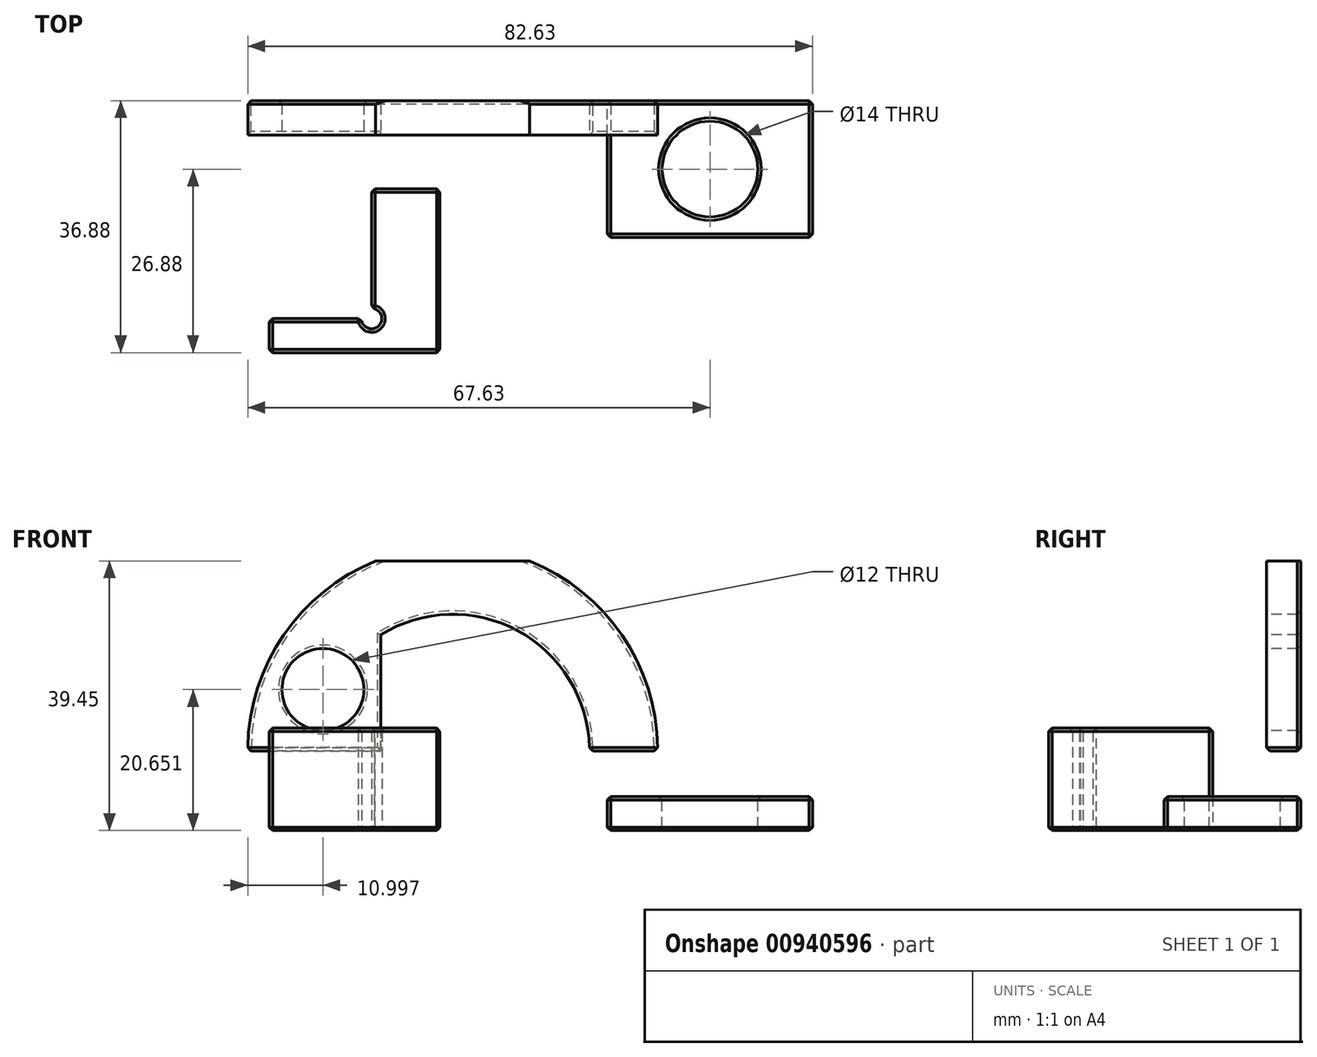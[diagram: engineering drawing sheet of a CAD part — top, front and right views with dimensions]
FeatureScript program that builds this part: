
annotation { "Feature Type Name" : "Feature", "Feature Type Description" : "" }
export const myFeature = defineFeature(function(context is Context, id is Id, definition is map)
    precondition{}
    {
        {
            var Q0;
            Q0=qCreatedBy(makeId("Front.planeOp"),FACE);
            var sketch = newSketch(context, id + "F0", { "sketchPlane" : qUnion([Q0])});
            skLineSegment(sketch, "E0.bottom", {"start": v(0, 0) * mm, "end": v(30, 0) * mm});
            skLineSegment(sketch, "E0.top", {"start": v(0, 5) * mm, "end": v(30, 5) * mm});
            skLineSegment(sketch, "E0.left", {"start": v(0, 0) * mm, "end": v(0, 5) * mm});
            skLineSegment(sketch, "E0.right", {"start": v(30, 0) * mm, "end": v(30, 5) * mm});
            skSolve(sketch);
        }
        {
            var Q0;
            Q0=makeQuery(id+"F0.imprint","IMPRINT",FACE,{"disambiguationData":[TD([[makeQuery(id+"F0.imprint","IMPRINT",EDGE,{"derivedFrom":sQuery(id+"F0.wireOp",EDGE,"E0.bottom")}),1.0]])]});
            extrude(context, id + "F1", {"entities" : qUnion([Q0]), "depth" : 20 * mm, "offsetDistance" : 25 * mm});
        }
        {
            var Q0;
            Q0=qCreatedBy(makeId("Front.planeOp"),FACE);
            var sketch = newSketch(context, id + "F2", { "sketchPlane" : qUnion([Q0])});
            skLineSegment(sketch, "E1.bottom", {"start": v(-52.63, 11.65) * mm, "end": v(7.37, 11.65) * mm});
            skLineSegment(sketch, "E1.top", {"start": v(-52.63, 39.45) * mm, "end": v(7.37, 39.45) * mm});
            skLineSegment(sketch, "E1.left", {"start": v(-52.63, 11.65) * mm, "end": v(-52.63, 39.45) * mm});
            skLineSegment(sketch, "E1.right", {"start": v(7.37, 11.65) * mm, "end": v(7.37, 39.45) * mm});
            skSolve(sketch);
        }
        {
            var Q0;
            Q0 = qSketchRegion(id + "F2", true);
            extrude(context, id + "F3", {"entities" : qUnion([Q0]), "depth" : 5 * mm, "offsetDistance" : 25 * mm});
        }
        {
            var Q0;
            Q0=makeQuery(id+"F3.opExtrude","CAP_FACE",FACE,{"disambiguationData":[OSD([sQuery(id+"F2.wireOp",EDGE,"E1.bottom"),sQuery(id+"F2.wireOp",EDGE,"E1.top"),sQuery(id+"F2.wireOp",EDGE,"E1.left"),sQuery(id+"F2.wireOp",EDGE,"E1.right")])],"isStart":false});
            var sketch = newSketch(context, id + "F4", { "sketchPlane" : qUnion([Q0])});
            skCircle(sketch, "E2", {"center": v(-22.63, 11.65) * mm, "radius": 20 * mm});
            skCircle(sketch, "E3", {"center": v(-22.63, 11.65) * mm, "radius": 30 * mm});
            skLineSegment(sketch, "E4", {"start": v(-33.17, 28.65) * mm, "end": v(-33.17, 11.65) * mm});
            skLineSegment(sketch, "E5", {"start": v(-33.17, 11.65) * mm, "end": v(-42.63, 11.65) * mm});
            skCircle(sketch, "E6", {"center": v(-41.63, 20.65) * mm, "radius": 6 * mm});
            skSolve(sketch);
        }
        {
            var Q0;
            {var subQ0=sQuery(id+"F4.wireOp",EDGE,"E2");var subQ1=makeQuery(id+"F3.opExtrude","CAP_EDGE",EDGE,{"disambiguationData":[OSD([sQuery(id+"F2.wireOp",EDGE,"E1.bottom")])],"isStart":false});var subQ2=makeQuery(id+"F4.imprint","INTERSECT",VERTEX,{"disambiguationData":[OD(0.0)],"derivedFrom":[subQ1,subQ0]});Q0=makeQuery(id+"F4.imprint","IMPRINT",FACE,{"disambiguationData":[TD([[makeQuery(id+"F4.imprint","IMPRINT",EDGE,{"disambiguationData":[TD([[subQ2,-1.0]])],"derivedFrom":subQ0}),1.0]])]});}
            var Q1;
            {var subQ0=sQuery(id+"F4.wireOp",EDGE,"E2");var subQ1=makeQuery(id+"F3.opExtrude","CAP_EDGE",EDGE,{"disambiguationData":[OSD([sQuery(id+"F2.wireOp",EDGE,"E1.bottom")])],"isStart":false});var subQ2=makeQuery(id+"F4.imprint","INTERSECT",VERTEX,{"disambiguationData":[OD(0.0)],"derivedFrom":[subQ1,subQ0]});Q1=makeQuery(id+"F4.imprint","IMPRINT",FACE,{"disambiguationData":[TD([[makeQuery(id+"F4.imprint","IMPRINT",EDGE,{"disambiguationData":[TD([[subQ2,1.0]])],"derivedFrom":subQ0}),1.0]])]});}
            var Q2;
            {var subQ1=makeQuery(id+"F3.opExtrude","CAP_EDGE",EDGE,{"disambiguationData":[OSD([sQuery(id+"F2.wireOp",EDGE,"E1.left")])],"isStart":false});Q2=makeQuery(id+"F4.imprint","IMPRINT",FACE,{"disambiguationData":[TD([[makeQuery(id+"F4.imprint","IMPRINT",EDGE,{"derivedFrom":subQ1}),-1.0]])]});}
            var Q3;
            {var subQ1=makeQuery(id+"F3.opExtrude","CAP_EDGE",EDGE,{"disambiguationData":[OSD([sQuery(id+"F2.wireOp",EDGE,"E1.right")])],"isStart":false});Q3=makeQuery(id+"F4.imprint","IMPRINT",FACE,{"disambiguationData":[TD([[makeQuery(id+"F4.imprint","IMPRINT",EDGE,{"derivedFrom":subQ1}),1.0]])]});}
            var Q4;
            {var subQ0=sQuery(id+"F4.wireOp",EDGE,"E6");var subQ1=sQuery(id+"F4.wireOp",EDGE,"E2");var subQ2=makeQuery(id+"F4.imprint","INTERSECT",VERTEX,{"disambiguationData":[OD(0.0)],"derivedFrom":[subQ1,subQ0]});Q4=makeQuery(id+"F4.imprint","IMPRINT",FACE,{"disambiguationData":[TD([[makeQuery(id+"F4.imprint","IMPRINT",EDGE,{"disambiguationData":[TD([[subQ2,-1.0]])],"derivedFrom":subQ1}),1.0]])]});}
            var Q5;
            {var subQ0=sQuery(id+"F4.wireOp",EDGE,"E6");var subQ1=sQuery(id+"F4.wireOp",EDGE,"E2");var subQ2=makeQuery(id+"F4.imprint","INTERSECT",VERTEX,{"disambiguationData":[OD(0.0)],"derivedFrom":[subQ1,subQ0]});Q5=makeQuery(id+"F4.imprint","IMPRINT",FACE,{"disambiguationData":[TD([[makeQuery(id+"F4.imprint","IMPRINT",EDGE,{"disambiguationData":[TD([[subQ2,-1.0]])],"derivedFrom":subQ1}),-1.0]])]});}
            extrude(context, id + "F5", {"entities" : qUnion([Q0, Q1, Q2, Q3, Q4, Q5]), "operationType" : NewBodyOperationType.REMOVE, "oppositeDirection" : true, "depth" : 25 * mm, "offsetDistance" : 25 * mm});
        }
        {
            var Q0;
            Q0=qCreatedBy(makeId("Top.planeOp"),FACE);
            var sketch = newSketch(context, id + "F6", { "sketchPlane" : qUnion([Q0])});
            skLineSegment(sketch, "E7.bottom", {"start": v(-49.5, -36.88) * mm, "end": v(-24.5, -36.88) * mm});
            skLineSegment(sketch, "E7.top", {"start": v(-34.5, -12.88) * mm, "end": v(-24.5, -12.88) * mm});
            skLineSegment(sketch, "E7.left", {"start": v(-49.5, -36.88) * mm, "end": v(-49.5, -31.88) * mm});
            skLineSegment(sketch, "E7.right", {"start": v(-24.5, -36.88) * mm, "end": v(-24.5, -12.88) * mm});
            skLineSegment(sketch, "E8.top", {"start": v(-49.5, -31.88) * mm, "end": v(-36, -31.88) * mm});
            skLineSegment(sketch, "E8.right", {"start": v(-34.5, -12.88) * mm, "end": v(-34.5, -30.38) * mm});
            skArc(sketch, "E9", {"start": v(-36, -31.88) * mm, "mid": v(-33.45, -32.94) * mm, "end": v(-34.5, -30.38) * mm});
            skSolve(sketch);
        }
        {
            var Q0;
            Q0=makeQuery(id+"F6.imprint","IMPRINT",FACE,{"disambiguationData":[TD([[makeQuery(id+"F6.imprint","IMPRINT",EDGE,{"derivedFrom":sQuery(id+"F6.wireOp",EDGE,"E7.bottom")}),1.0]])]});
            extrude(context, id + "F7", {"entities" : qUnion([Q0]), "depth" : 15 * mm, "offsetDistance" : 25 * mm});
        }
        {
            var Q0;
            Q0=makeQuery(id+"F1.opExtrude","SWEPT_FACE",FACE,{"disambiguationData":[OSD([sQuery(id+"F0.wireOp",EDGE,"E0.top")])]});
            var sketch = newSketch(context, id + "F8", { "sketchPlane" : qUnion([Q0])});
            skCircle(sketch, "E10", {"center": v(15, -10) * mm, "radius": 7 * mm});
            skSolve(sketch);
        }
        {
            var Q0;
            Q0=makeQuery(id+"F8.imprint","IMPRINT",FACE,{"disambiguationData":[TD([[makeQuery(id+"F8.imprint","IMPRINT",EDGE,{"derivedFrom":sQuery(id+"F8.wireOp",EDGE,"E10")}),1.0]])]});
            extrude(context, id + "F9", {"entities" : qUnion([Q0]), "operationType" : NewBodyOperationType.REMOVE, "oppositeDirection" : true, "depth" : 25 * mm, "offsetDistance" : 25 * mm});
        }
        {
            var Q0;
            Q0=makeQuery(id+"F1.opExtrude","SWEPT_FACE",FACE,{"disambiguationData":[OSD([sQuery(id+"F0.wireOp",EDGE,"E0.bottom")])]});
            var Q1;
            Q1=makeQuery(id+"F1.opExtrude","SWEPT_EDGE",EDGE,{"disambiguationData":[OSD([sQuery(id+"F0.wireOp",EDGE,"E0.bottom"),sQuery(id+"F0.wireOp",EDGE,"E0.right")])]});
            var Q2;
            Q2=makeQuery(id+"F1.opExtrude","CAP_FACE",FACE,{"disambiguationData":[OSD([sQuery(id+"F0.wireOp",EDGE,"E0.bottom"),sQuery(id+"F0.wireOp",EDGE,"E0.top"),sQuery(id+"F0.wireOp",EDGE,"E0.left"),sQuery(id+"F0.wireOp",EDGE,"E0.right")])],"isStart":true});
            var Q3;
            Q3=makeQuery(id+"F1.opExtrude","SWEPT_EDGE",EDGE,{"disambiguationData":[OSD([sQuery(id+"F0.wireOp",EDGE,"E0.top"),sQuery(id+"F0.wireOp",EDGE,"E0.left")])]});
            var Q4;
            Q4=makeQuery(id+"F1.opExtrude","CAP_FACE",FACE,{"disambiguationData":[OSD([sQuery(id+"F0.wireOp",EDGE,"E0.bottom"),sQuery(id+"F0.wireOp",EDGE,"E0.top"),sQuery(id+"F0.wireOp",EDGE,"E0.left"),sQuery(id+"F0.wireOp",EDGE,"E0.right")])],"isStart":false});
            var Q5;
            Q5=makeQuery(id+"F1.opExtrude","SWEPT_EDGE",EDGE,{"disambiguationData":[OSD([sQuery(id+"F0.wireOp",EDGE,"E0.top"),sQuery(id+"F0.wireOp",EDGE,"E0.right")])]});
            var Q6;
            Q6=makeQuery(id+"F1.opExtrude","SWEPT_FACE",FACE,{"disambiguationData":[OSD([sQuery(id+"F0.wireOp",EDGE,"E0.top")])]});
            var Q7;
            Q7=makeQuery(id+"F1.opExtrude","SWEPT_FACE",FACE,{"disambiguationData":[OSD([sQuery(id+"F0.wireOp",EDGE,"E0.left")])]});
            var Q8;
            Q8=makeQuery(id+"F1.opExtrude","SWEPT_FACE",FACE,{"disambiguationData":[OSD([sQuery(id+"F0.wireOp",EDGE,"E0.right")])]});
            var Q9;
            Q9=makeQuery(id+"F1.opExtrude","CAP_EDGE",EDGE,{"disambiguationData":[OSD([sQuery(id+"F0.wireOp",EDGE,"E0.top")])],"isStart":true});
            var Q10;
            Q10=makeQuery(id+"F1.opExtrude","CAP_EDGE",EDGE,{"disambiguationData":[OSD([sQuery(id+"F0.wireOp",EDGE,"E0.top")])],"isStart":false});
            var Q11;
            Q11=makeQuery(id+"F1.opExtrude","SWEPT_EDGE",EDGE,{"disambiguationData":[OSD([sQuery(id+"F0.wireOp",EDGE,"E0.bottom"),sQuery(id+"F0.wireOp",EDGE,"E0.left")])]});
            var Q12;
            Q12=makeQuery(id+"F1.opExtrude","CAP_EDGE",EDGE,{"disambiguationData":[OSD([sQuery(id+"F0.wireOp",EDGE,"E0.bottom")])],"isStart":true});
            var Q13;
            Q13=makeQuery(id+"F1.opExtrude","CAP_EDGE",EDGE,{"disambiguationData":[OSD([sQuery(id+"F0.wireOp",EDGE,"E0.bottom")])],"isStart":false});
            var Q14;
            Q14=makeQuery(id+"F1.opExtrude","CAP_EDGE",EDGE,{"disambiguationData":[OSD([sQuery(id+"F0.wireOp",EDGE,"E0.left")])],"isStart":true});
            var Q15;
            Q15=makeQuery(id+"F1.opExtrude","CAP_EDGE",EDGE,{"disambiguationData":[OSD([sQuery(id+"F0.wireOp",EDGE,"E0.left")])],"isStart":false});
            var Q16;
            Q16=makeQuery(id+"F1.opExtrude","CAP_EDGE",EDGE,{"disambiguationData":[OSD([sQuery(id+"F0.wireOp",EDGE,"E0.right")])],"isStart":true});
            var Q17;
            Q17=makeQuery(id+"F1.opExtrude","CAP_EDGE",EDGE,{"disambiguationData":[OSD([sQuery(id+"F0.wireOp",EDGE,"E0.right")])],"isStart":false});
            var Q18;
            {var subQ0=sQuery(id+"F4.wireOp",EDGE,"E3");var subQ1=sQuery(id+"F2.wireOp",EDGE,"E1.left");var subQ2=sQuery(id+"F2.wireOp",EDGE,"E1.bottom");var subQ3=sQuery(id+"F2.wireOp",EDGE,"E1.top");Q18=makeQuery(id+"F5.boolean.opBoolean","INTERSECT",EDGE,{"derivedFrom":[makeQuery(id+"F3.opExtrude","CAP_FACE",FACE,{"disambiguationData":[OSD([subQ2,subQ3,subQ1,sQuery(id+"F2.wireOp",EDGE,"E1.right")])],"isStart":true}),makeQuery(id+"F5.opExtrude","SWEPT_FACE",FACE,{"disambiguationData":[OSD([subQ0]),TDD([makeQuery(id+"F4.imprint","IMPRINT",EDGE,{"disambiguationData":[TD([[makeQuery(id+"F4.imprint","INTERSECT",VERTEX,{"disambiguationData":[OD(1.0)],"derivedFrom":[makeQuery(id+"F3.opExtrude","CAP_EDGE",EDGE,{"disambiguationData":[OSD([subQ3])],"isStart":false}),subQ0]}),-1.0]])],"derivedFrom":subQ0})])]})]});}
            var Q19;
            Q19=makeQuery(id+"F5.boolean.opBoolean","INTERSECT",EDGE,{"derivedFrom":[makeQuery(id+"F3.opExtrude","CAP_FACE",FACE,{"disambiguationData":[OSD([sQuery(id+"F2.wireOp",EDGE,"E1.bottom"),sQuery(id+"F2.wireOp",EDGE,"E1.top"),sQuery(id+"F2.wireOp",EDGE,"E1.left"),sQuery(id+"F2.wireOp",EDGE,"E1.right")])],"isStart":true}),makeQuery(id+"F5.opExtrude","SWEPT_FACE",FACE,{"disambiguationData":[OSD([sQuery(id+"F4.wireOp",EDGE,"E2")])]})]});
            var Q20;
            {var subQ0=sQuery(id+"F4.wireOp",EDGE,"E3");var subQ1=sQuery(id+"F2.wireOp",EDGE,"E1.top");Q20=makeQuery(id+"F5.boolean.opBoolean","COPY",EDGE,{"derivedFrom":makeQuery(id+"F5.opExtrude","SWEPT_EDGE",EDGE,{"disambiguationData":[OSD([subQ1,subQ0]),TDD([makeQuery(id+"F4.imprint","INTERSECT",VERTEX,{"disambiguationData":[OD(1.0)],"derivedFrom":[makeQuery(id+"F3.opExtrude","CAP_EDGE",EDGE,{"disambiguationData":[OSD([subQ1])],"isStart":false}),subQ0]})])]})});}
            var Q21;
            {var subQ0=sQuery(id+"F4.wireOp",EDGE,"E3");Q21=makeQuery(id+"F5.boolean.opBoolean","COPY",EDGE,{"derivedFrom":makeQuery(id+"F5.opExtrude","CAP_EDGE",EDGE,{"disambiguationData":[OSD([subQ0]),TDD([makeQuery(id+"F4.imprint","IMPRINT",EDGE,{"disambiguationData":[TD([[makeQuery(id+"F4.imprint","INTERSECT",VERTEX,{"disambiguationData":[OD(1.0)],"derivedFrom":[makeQuery(id+"F3.opExtrude","CAP_EDGE",EDGE,{"disambiguationData":[OSD([sQuery(id+"F2.wireOp",EDGE,"E1.top")])],"isStart":false}),subQ0]}),-1.0]])],"derivedFrom":subQ0})])],"isStart":true})});}
            var Q22;
            {var subQ0=sQuery(id+"F4.wireOp",EDGE,"E3");Q22=makeQuery(id+"F5.boolean.opBoolean","COPY",EDGE,{"derivedFrom":makeQuery(id+"F5.opExtrude","CAP_EDGE",EDGE,{"disambiguationData":[OSD([subQ0]),TDD([makeQuery(id+"F4.imprint","IMPRINT",EDGE,{"disambiguationData":[TD([[makeQuery(id+"F4.imprint","INTERSECT",VERTEX,{"disambiguationData":[OD(0.0)],"derivedFrom":[makeQuery(id+"F3.opExtrude","CAP_EDGE",EDGE,{"disambiguationData":[OSD([sQuery(id+"F2.wireOp",EDGE,"E1.top")])],"isStart":false}),subQ0]}),1.0]])],"derivedFrom":subQ0})])],"isStart":true})});}
            var Q23;
            Q23=makeQuery(id+"F5.boolean.opBoolean","COPY",EDGE,{"derivedFrom":makeQuery(id+"F5.opExtrude","CAP_EDGE",EDGE,{"disambiguationData":[OSD([sQuery(id+"F4.wireOp",EDGE,"E2")])],"isStart":true})});
            var Q24;
            {var subQ0=sQuery(id+"F2.wireOp",EDGE,"E1.left");var subQ1=sQuery(id+"F2.wireOp",EDGE,"E1.bottom");Q24=makeQuery(id+"F5.boolean.opBoolean","MERGE",EDGE,{"derivedFrom":[makeQuery(id+"F3.opExtrude","SWEPT_EDGE",EDGE,{"disambiguationData":[OSD([subQ1,subQ0])]})],"fromTools":[makeQuery(id+"F5.opExtrude","SWEPT_EDGE",EDGE,{"disambiguationData":[OSD([subQ1,subQ0,sQuery(id+"F4.wireOp",EDGE,"E3")])]})]});}
            var Q25;
            Q25=makeQuery(id+"F5.boolean.opBoolean","INTERSECT",EDGE,{"disambiguationData":[OD(0.0)],"derivedFrom":[makeQuery(id+"F3.opExtrude","SWEPT_FACE",FACE,{"disambiguationData":[OSD([sQuery(id+"F2.wireOp",EDGE,"E1.bottom")])]}),makeQuery(id+"F5.opExtrude","SWEPT_FACE",FACE,{"disambiguationData":[OSD([sQuery(id+"F4.wireOp",EDGE,"E2")])]})]});
            var Q26;
            Q26=makeQuery(id+"F5.boolean.opBoolean","INTERSECT",EDGE,{"disambiguationData":[OD(1.0)],"derivedFrom":[makeQuery(id+"F3.opExtrude","SWEPT_FACE",FACE,{"disambiguationData":[OSD([sQuery(id+"F2.wireOp",EDGE,"E1.bottom")])]}),makeQuery(id+"F5.opExtrude","SWEPT_FACE",FACE,{"disambiguationData":[OSD([sQuery(id+"F4.wireOp",EDGE,"E2")])]})]});
            var Q27;
            {var subQ0=sQuery(id+"F4.wireOp",EDGE,"E3");var subQ1=sQuery(id+"F2.wireOp",EDGE,"E1.top");Q27=makeQuery(id+"F5.boolean.opBoolean","COPY",EDGE,{"derivedFrom":makeQuery(id+"F5.opExtrude","SWEPT_EDGE",EDGE,{"disambiguationData":[OSD([subQ1,subQ0]),TDD([makeQuery(id+"F4.imprint","INTERSECT",VERTEX,{"disambiguationData":[OD(0.0)],"derivedFrom":[makeQuery(id+"F3.opExtrude","CAP_EDGE",EDGE,{"disambiguationData":[OSD([subQ1])],"isStart":false}),subQ0]})])]})});}
            var Q28;
            {var subQ0=sQuery(id+"F4.wireOp",EDGE,"E3");var subQ1=sQuery(id+"F2.wireOp",EDGE,"E1.right");var subQ2=sQuery(id+"F2.wireOp",EDGE,"E1.bottom");var subQ3=sQuery(id+"F2.wireOp",EDGE,"E1.top");Q28=makeQuery(id+"F5.boolean.opBoolean","INTERSECT",EDGE,{"derivedFrom":[makeQuery(id+"F3.opExtrude","CAP_FACE",FACE,{"disambiguationData":[OSD([subQ2,subQ3,sQuery(id+"F2.wireOp",EDGE,"E1.left"),subQ1])],"isStart":true}),makeQuery(id+"F5.opExtrude","SWEPT_FACE",FACE,{"disambiguationData":[OSD([subQ0]),TDD([makeQuery(id+"F4.imprint","IMPRINT",EDGE,{"disambiguationData":[TD([[makeQuery(id+"F4.imprint","INTERSECT",VERTEX,{"disambiguationData":[OD(0.0)],"derivedFrom":[makeQuery(id+"F3.opExtrude","CAP_EDGE",EDGE,{"disambiguationData":[OSD([subQ3])],"isStart":false}),subQ0]}),1.0]])],"derivedFrom":subQ0})])]})]});}
            var Q29;
            {var subQ0=sQuery(id+"F2.wireOp",EDGE,"E1.right");var subQ1=sQuery(id+"F2.wireOp",EDGE,"E1.bottom");Q29=makeQuery(id+"F5.boolean.opBoolean","MERGE",EDGE,{"derivedFrom":[makeQuery(id+"F3.opExtrude","SWEPT_EDGE",EDGE,{"disambiguationData":[OSD([subQ1,subQ0])]})],"fromTools":[makeQuery(id+"F5.opExtrude","SWEPT_EDGE",EDGE,{"disambiguationData":[OSD([subQ1,subQ0,sQuery(id+"F4.wireOp",EDGE,"E3")])]})]});}
            var Q30;
            Q30=makeQuery(id+"F7.opExtrude","CAP_EDGE",EDGE,{"disambiguationData":[OSD([sQuery(id+"F6.wireOp",EDGE,"E9")])],"isStart":false});
            var Q31;
            Q31=makeQuery(id+"F7.opExtrude","SWEPT_EDGE",EDGE,{"disambiguationData":[OSD([sQuery(id+"F6.wireOp",EDGE,"E7.top"),sQuery(id+"F6.wireOp",EDGE,"E7.right")])]});
            var Q32;
            Q32=makeQuery(id+"F7.opExtrude","SWEPT_EDGE",EDGE,{"disambiguationData":[OSD([sQuery(id+"F6.wireOp",EDGE,"E7.bottom"),sQuery(id+"F6.wireOp",EDGE,"E7.right")])]});
            var Q33;
            Q33=makeQuery(id+"F7.opExtrude","SWEPT_EDGE",EDGE,{"disambiguationData":[OSD([sQuery(id+"F6.wireOp",EDGE,"E7.bottom"),sQuery(id+"F6.wireOp",EDGE,"E7.left")])]});
            var Q34;
            {var subQ0=sQuery(id+"F2.wireOp",EDGE,"E1.bottom");var subQ2=sQuery(id+"F2.wireOp",EDGE,"E1.top");var subQ3=sQuery(id+"F4.wireOp",EDGE,"E3");var subQ4=makeQuery(id+"F3.opExtrude","CAP_EDGE",EDGE,{"disambiguationData":[OSD([subQ0])],"isStart":false});Q34=makeQuery(id+"F5.boolean.opBoolean","SPLIT",EDGE,{"disambiguationData":[TD([makeQuery(id+"F5.opExtrude","SWEPT_FACE",FACE,{"disambiguationData":[OSD([subQ3]),TDD([makeQuery(id+"F4.imprint","IMPRINT",EDGE,{"disambiguationData":[TD([[makeQuery(id+"F4.imprint","INTERSECT",VERTEX,{"disambiguationData":[OD(1.0)],"derivedFrom":[makeQuery(id+"F3.opExtrude","CAP_EDGE",EDGE,{"disambiguationData":[OSD([subQ2])],"isStart":false}),subQ3]}),-1.0]])],"derivedFrom":subQ3})])]})])],"derivedFrom":subQ4});}
            var Q35;
            Q35=makeQuery(id+"F7.opExtrude","CAP_EDGE",EDGE,{"disambiguationData":[OSD([sQuery(id+"F6.wireOp",EDGE,"E8.right")])],"isStart":false});
            var Q36;
            Q36=makeQuery(id+"F7.opExtrude","CAP_EDGE",EDGE,{"disambiguationData":[OSD([sQuery(id+"F6.wireOp",EDGE,"E7.right")])],"isStart":false});
            var Q37;
            Q37=makeQuery(id+"F7.opExtrude","SWEPT_EDGE",EDGE,{"disambiguationData":[OSD([sQuery(id+"F6.wireOp",EDGE,"E7.top"),sQuery(id+"F6.wireOp",EDGE,"E8.right")])]});
            var Q38;
            Q38=makeQuery(id+"F7.opExtrude","CAP_EDGE",EDGE,{"disambiguationData":[OSD([sQuery(id+"F6.wireOp",EDGE,"E7.left")])],"isStart":false});
            var Q39;
            Q39=makeQuery(id+"F7.opExtrude","CAP_EDGE",EDGE,{"disambiguationData":[OSD([sQuery(id+"F6.wireOp",EDGE,"E8.top")])],"isStart":false});
            var Q40;
            Q40=makeQuery(id+"F7.opExtrude","CAP_EDGE",EDGE,{"disambiguationData":[OSD([sQuery(id+"F6.wireOp",EDGE,"E7.bottom")])],"isStart":false});
            var Q41;
            Q41=makeQuery(id+"F7.opExtrude","SWEPT_EDGE",EDGE,{"disambiguationData":[OSD([sQuery(id+"F6.wireOp",EDGE,"E7.left"),sQuery(id+"F6.wireOp",EDGE,"E8.top")])]});
            var Q42;
            Q42=makeQuery(id+"F7.opExtrude","CAP_EDGE",EDGE,{"disambiguationData":[OSD([sQuery(id+"F6.wireOp",EDGE,"E7.bottom")])],"isStart":true});
            var Q43;
            Q43=makeQuery(id+"F7.opExtrude","CAP_EDGE",EDGE,{"disambiguationData":[OSD([sQuery(id+"F6.wireOp",EDGE,"E7.left")])],"isStart":true});
            var Q44;
            Q44=makeQuery(id+"F7.opExtrude","SWEPT_EDGE",EDGE,{"disambiguationData":[OSD([sQuery(id+"F6.wireOp",EDGE,"E8.top"),sQuery(id+"F6.wireOp",EDGE,"E9")])]});
            var Q45;
            Q45=makeQuery(id+"F7.opExtrude","CAP_EDGE",EDGE,{"disambiguationData":[OSD([sQuery(id+"F6.wireOp",EDGE,"E7.right")])],"isStart":true});
            var Q46;
            Q46=makeQuery(id+"F7.opExtrude","CAP_EDGE",EDGE,{"disambiguationData":[OSD([sQuery(id+"F6.wireOp",EDGE,"E7.top")])],"isStart":true});
            var Q47;
            Q47=makeQuery(id+"F7.opExtrude","CAP_EDGE",EDGE,{"disambiguationData":[OSD([sQuery(id+"F6.wireOp",EDGE,"E7.top")])],"isStart":false});
            var Q48;
            Q48=makeQuery(id+"F7.opExtrude","CAP_EDGE",EDGE,{"disambiguationData":[OSD([sQuery(id+"F6.wireOp",EDGE,"E9")])],"isStart":true});
            var Q49;
            Q49=makeQuery(id+"F7.opExtrude","SWEPT_EDGE",EDGE,{"disambiguationData":[OSD([sQuery(id+"F6.wireOp",EDGE,"E8.right"),sQuery(id+"F6.wireOp",EDGE,"E9")])]});
            var Q50;
            Q50=makeQuery(id+"F7.opExtrude","CAP_EDGE",EDGE,{"disambiguationData":[OSD([sQuery(id+"F6.wireOp",EDGE,"E8.top")])],"isStart":true});
            var Q51;
            Q51=makeQuery(id+"F7.opExtrude","CAP_EDGE",EDGE,{"disambiguationData":[OSD([sQuery(id+"F6.wireOp",EDGE,"E8.right")])],"isStart":true});
            var Q52;
            Q52=makeQuery(id+"F5.boolean.opBoolean","COPY",EDGE,{"derivedFrom":makeQuery(id+"F5.opExtrude","CAP_EDGE",EDGE,{"disambiguationData":[OSD([sQuery(id+"F4.wireOp",EDGE,"E4")])],"isStart":true})});
            var Q53;
            Q53=makeQuery(id+"F5.boolean.opBoolean","INTERSECT",EDGE,{"derivedFrom":[makeQuery(id+"F3.opExtrude","CAP_FACE",FACE,{"disambiguationData":[OSD([sQuery(id+"F2.wireOp",EDGE,"E1.bottom"),sQuery(id+"F2.wireOp",EDGE,"E1.top"),sQuery(id+"F2.wireOp",EDGE,"E1.left"),sQuery(id+"F2.wireOp",EDGE,"E1.right")])],"isStart":true}),makeQuery(id+"F5.opExtrude","SWEPT_FACE",FACE,{"disambiguationData":[OSD([sQuery(id+"F4.wireOp",EDGE,"E4")])]})]});
            var Q54;
            {var subQ0=sQuery(id+"F2.wireOp",EDGE,"E1.bottom");Q54=makeQuery(id+"F5.boolean.opBoolean","SPLIT",EDGE,{"disambiguationData":[TD([makeQuery(id+"F5.opExtrude","SWEPT_FACE",FACE,{"disambiguationData":[OSD([sQuery(id+"F4.wireOp",EDGE,"E4")])]})])],"derivedFrom":makeQuery(id+"F3.opExtrude","CAP_EDGE",EDGE,{"disambiguationData":[OSD([subQ0])],"isStart":true})});}
            var Q55;
            {var subQ0=sQuery(id+"F2.wireOp",EDGE,"E1.bottom");Q55=makeQuery(id+"F5.boolean.opBoolean","SPLIT",EDGE,{"disambiguationData":[TD([makeQuery(id+"F5.opExtrude","SWEPT_FACE",FACE,{"disambiguationData":[OSD([sQuery(id+"F4.wireOp",EDGE,"E2")])]})])],"derivedFrom":makeQuery(id+"F3.opExtrude","CAP_EDGE",EDGE,{"disambiguationData":[OSD([subQ0])],"isStart":true})});}
            var Q56;
            {var subQ0=sQuery(id+"F2.wireOp",EDGE,"E1.bottom");var subQ4=makeQuery(id+"F3.opExtrude","CAP_EDGE",EDGE,{"disambiguationData":[OSD([subQ0])],"isStart":false});Q56=makeQuery(id+"F5.boolean.opBoolean","SPLIT",EDGE,{"disambiguationData":[TD([makeQuery(id+"F5.opExtrude","SWEPT_FACE",FACE,{"disambiguationData":[OSD([sQuery(id+"F4.wireOp",EDGE,"E2")])]})])],"derivedFrom":subQ4});}
            var Q57;
            Q57=makeQuery(id+"F5.boolean.opBoolean","COPY",EDGE,{"derivedFrom":makeQuery(id+"F5.opExtrude","CAP_EDGE",EDGE,{"disambiguationData":[OSD([sQuery(id+"F4.wireOp",EDGE,"E6")])],"isStart":true})});
            var Q58;
            Q58=makeQuery(id+"F5.boolean.opBoolean","INTERSECT",EDGE,{"derivedFrom":[makeQuery(id+"F3.opExtrude","CAP_FACE",FACE,{"disambiguationData":[OSD([sQuery(id+"F2.wireOp",EDGE,"E1.bottom"),sQuery(id+"F2.wireOp",EDGE,"E1.top"),sQuery(id+"F2.wireOp",EDGE,"E1.left"),sQuery(id+"F2.wireOp",EDGE,"E1.right")])],"isStart":true}),makeQuery(id+"F5.opExtrude","SWEPT_FACE",FACE,{"disambiguationData":[OSD([sQuery(id+"F4.wireOp",EDGE,"E6")])]})]});
            chamfer(context, id + "F10", {"entities" : qUnion([Q0, Q1, Q2, Q3, Q4, Q5, Q6, Q7, Q8, Q9, Q10, Q11, Q12, Q13, Q14, Q15, Q16, Q17, Q18, Q19, Q20, Q21, Q22, Q23, Q24, Q25, Q26, Q27, Q28, Q29, Q30, Q31, Q32, Q33, Q34, Q35, Q36, Q37, Q38, Q39, Q40, Q41, Q42, Q43, Q44, Q45, Q46, Q47, Q48, Q49, Q50, Q51, Q52, Q53, Q54, Q55, Q56, Q57, Q58]), "width" : 0.5 * mm, "tangentPropagation" : true});
        }
    });
